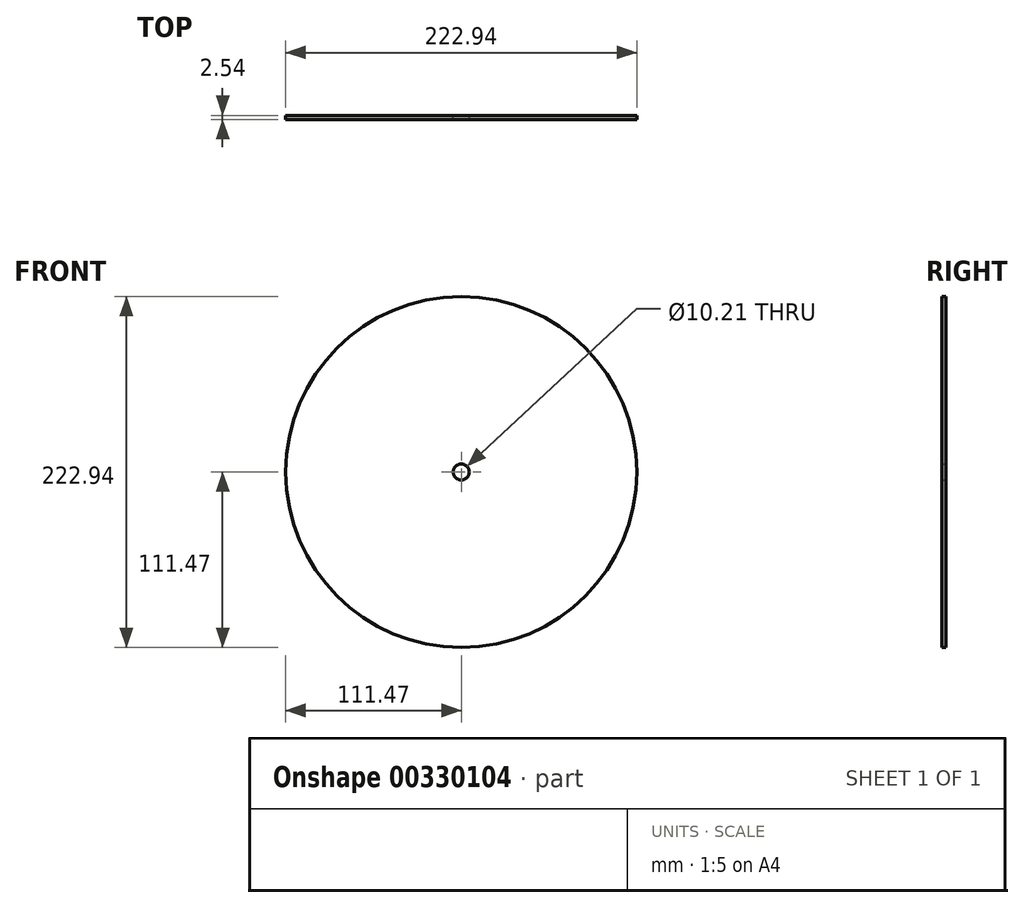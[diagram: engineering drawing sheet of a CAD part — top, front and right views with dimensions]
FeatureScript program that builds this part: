
annotation { "Feature Type Name" : "Feature", "Feature Type Description" : "" }
export const myFeature = defineFeature(function(context is Context, id is Id, definition is map)
    precondition{}
    {
        {
            var Q0;
            Q0=qCreatedBy(makeId("Front.planeOp"),FACE);
            var sketch = newSketch(context, id + "F0", { "sketchPlane" : qUnion([Q0])});
            skCircle(sketch, "E0", {"center": v(0, 0) * mm, "radius": 111.47 * mm});
            skCircle(sketch, "E1", {"center": v(0, 0) * mm, "radius": 40.6 * mm});
            skCircle(sketch, "E2", {"center": v(0, 0) * mm, "radius": 5.1 * mm});
            skSolve(sketch);
        }
        {
            var Q0;
            Q0=makeQuery(id+"F0.imprint","IMPRINT",FACE,{"disambiguationData":[TD([[makeQuery(id+"F0.imprint","IMPRINT",EDGE,{"derivedFrom":sQuery(id+"F0.wireOp",EDGE,"E0")}),1.0]])]});
            var Q1;
            Q1=makeQuery(id+"F0.imprint","IMPRINT",FACE,{"disambiguationData":[TD([[makeQuery(id+"F0.imprint","IMPRINT",EDGE,{"derivedFrom":sQuery(id+"F0.wireOp",EDGE,"E1")}),1.0]])]});
            extrude(context, id + "F1", {"entities" : qUnion([Q0, Q1]), "endBound" : BoundingType.SYMMETRIC, "depth" : 2.54 * mm});
        }
    });
